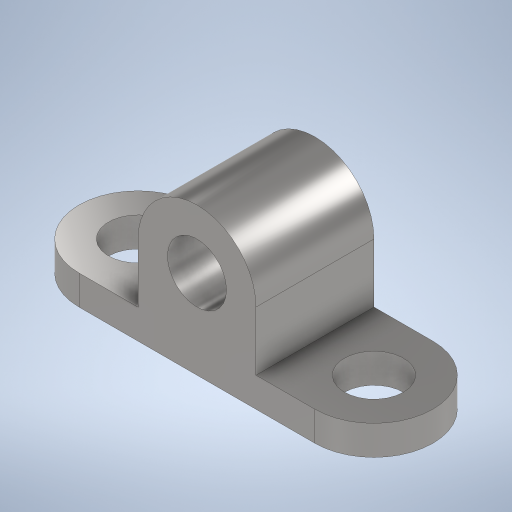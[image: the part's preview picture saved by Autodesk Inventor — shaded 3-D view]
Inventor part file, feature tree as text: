
AUTODESK INVENTOR PART (.ipt)
format: ipt  version: 2024 (Build 280153000, 153)  size: 281,088 bytes
history: native  units: mm
features: sketch x5, hole x3, extrude x2
ambient origin geometry x8: Origin, YZ Plane, XZ Plane, XY Plane, X Axis, Y Axis, Z Axis, Center Point
bodies: Volumenkörper1 (feature_tree)
feature tree (10):
  extrude  "Extrusion1"  Depth=40.0mm
  extrude  "Extrusion2"  Depth=20.0mm
  hole  "Bohrung1"  [1 undecoded]
  hole  "Bohrung2"  [1 undecoded]
  hole  "Bohrung3"  [1 undecoded]
  sketch  "Skizze1"  dims[d0=80.0mm d1=40.0mm]
  sketch  "Skizze3"  dims[d2=10.0mm d3=0.0mm d4=20.0mm]
  sketch  "Skizze4"  dims[d5=20.0mm d6=10.0mm d7=0.0mm]
  sketch  "Skizze5"  dims[d8=20.0mm d9=6.0mm d10=4.0mm d11=2.0mm d12=90.0deg d13=8.0mm d14=20.594885mm]
  sketch  "Skizze6"  dims[d15=20.0mm d16=6.0mm d17=4.0mm d18=2.0mm d19=90.0deg d20=8.0mm d21=20.594885mm d22=20.0mm d23=6.0mm d24=4.0mm d25=2.0mm d26=90.0deg d27=8.0mm d28=20.594885mm]
note: 3 required parameter values undecoded (feature->parameter linkage not recoverable at this tier; creation-order binding heuristic only, values carry confidence <= 0.55)
